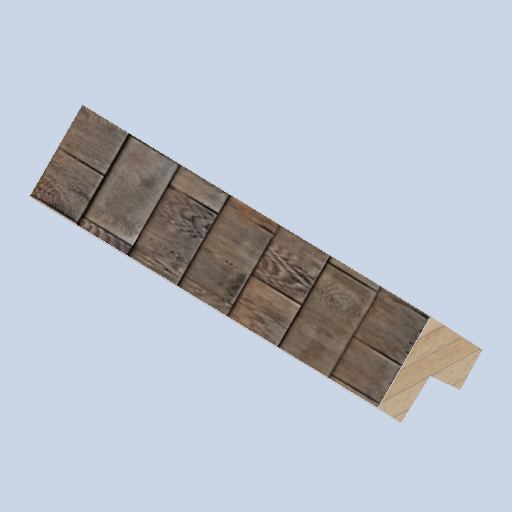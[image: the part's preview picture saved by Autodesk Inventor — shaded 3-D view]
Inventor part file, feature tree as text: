
AUTODESK INVENTOR PART (.ipt)
format: ipt  version: 2024.2 (Build 282272000, 272)  size: 244,736 bytes
history: native  units: in
note: dims shown in document units (in); Inventor stores cm internally (conversion verified against a paired STEP export)
features: sketch x8, plane x6, other x3
ambient origin geometry x8: Origin, YZ Plane, XZ Plane, XY Plane, X Axis, Y Axis, Z Axis, Center Point
bodies: Solid1 (feature_tree)
feature tree (17):
  other  "panel_pad_frame_01.ipt"
  other  "Solid1::panel_pad_frame_01.ipt"
  other  "TaggingFeature1"
  sketch  "Sketch1"  dims[d0=0.3937in]
  sketch  "Sketch2"
  sketch  "Sketch3"
  sketch  "Sketch6"
  sketch  "Sketch7"
  sketch  "Sketch8"
  sketch  "Sketch9"
  sketch  "Sketch10"
  plane  "Work Plane1"
  plane  "Work Plane2"
  plane  "Work Plane3"
  plane  "Work Plane4"
  plane  "Work Plane5"
  plane  "Work Plane6"
